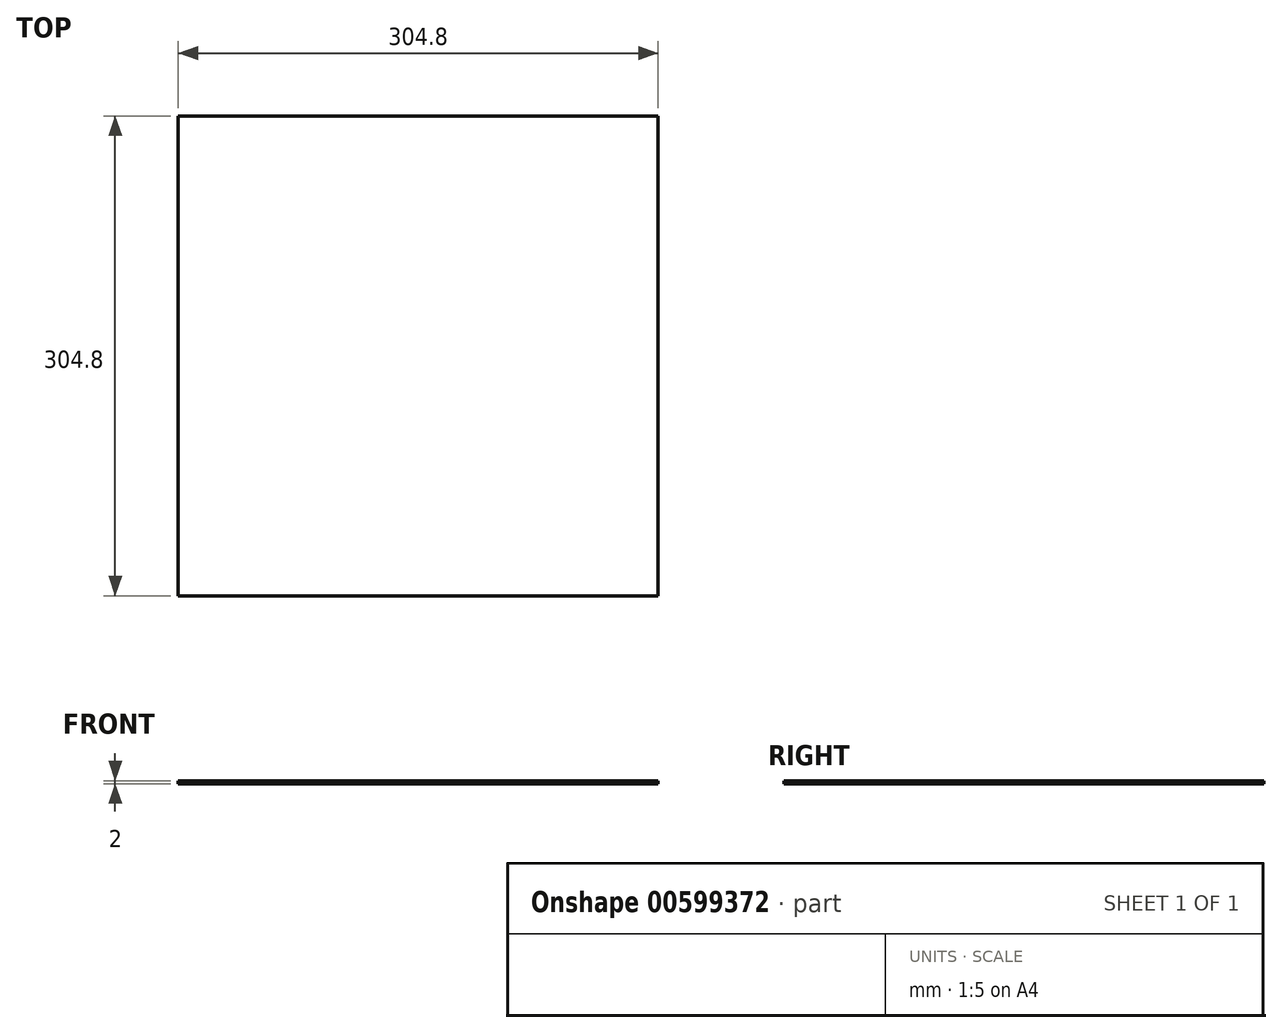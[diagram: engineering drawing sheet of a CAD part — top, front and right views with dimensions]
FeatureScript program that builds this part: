
annotation { "Feature Type Name" : "Feature", "Feature Type Description" : "" }
export const myFeature = defineFeature(function(context is Context, id is Id, definition is map)
    precondition{}
    {
        {
            var Q0;
            Q0=qCreatedBy(makeId("Top.planeOp"),FACE);
            var sketch = newSketch(context, id + "F0", { "sketchPlane" : qUnion([Q0])});
            skLineSegment(sketch, "E0.bottom", {"start": v(-152.4, 152.4) * mm, "end": v(152.4, 152.4) * mm});
            skLineSegment(sketch, "E0.top", {"start": v(-152.4, -152.4) * mm, "end": v(152.4, -152.4) * mm});
            skLineSegment(sketch, "E0.left", {"start": v(-152.4, 152.4) * mm, "end": v(-152.4, -152.4) * mm});
            skLineSegment(sketch, "E0.right", {"start": v(152.4, 152.4) * mm, "end": v(152.4, -152.4) * mm});
            skSolve(sketch);
        }
        {
            var Q0;
            Q0=qSketchRegion(id+"F0",true);
            extrude(context, id + "F1", {"entities" : qUnion([Q0]), "depth" : 2 * mm});
        }
    });
